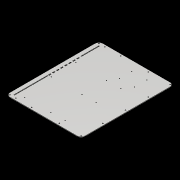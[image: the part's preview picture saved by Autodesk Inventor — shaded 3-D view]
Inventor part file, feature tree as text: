
AUTODESK INVENTOR PART (.ipt)
format: ipt  version: 2018.2 (Build 222227000, 227)  size: 322,560 bytes
history: native  units: mm
features: reference x21, other x7, extrude x7, sketch x7, projected_geometry x1
ambient origin geometry x8: Origin, YZ Plane, XZ Plane, XY Plane, X Axis, Y Axis, Z Axis, Center Point
bodies: Body1 (feature_tree)
feature tree (43):
  other  "ソリッド1"
  extrude  "押し出し1"  Depth=380.0mm
  extrude  "押し出し2"  Depth=470.0mm
  extrude  "押し出し3"  Depth=4.5mm
  extrude  "押し出し4"  Depth=10.0mm
  extrude  "押し出し5"  Depth=10.0mm
  extrude  "押し出し6"  Depth=10.0mm
  extrude  "押し出し7"  Depth=10.0mm
  sketch  "スケッチ1"
  sketch  "スケッチ2"
  reference  "参照1"
  reference  "参照2"
  reference  "参照3"
  reference  "参照4"
  reference  "参照5"
  reference  "参照6"
  reference  "参照7"
  reference  "参照8"
  reference  "参照9"
  sketch  "スケッチ4"
  reference  "参照10"
  reference  "参照11"
  reference  "参照12"
  reference  "参照13"
  reference  "参照14"
  reference  "参照15"
  reference  "参照16"
  reference  "参照17"
  reference  "参照18"
  reference  "参照19"
  sketch  "スケッチ5"
  sketch  "スケッチ6"
  projected_geometry  "投影ループ1"
  sketch  "スケッチ7"
  reference  "参照20"
  reference  "参照21"
  sketch  "スケッチ8"
  other  "<userpath>\Documents\CAD\eatx_case\layout.iam"
  other  "layout.iam"
  other  "Rampage V Extreme Assembly:1"
  other  "Rampage V Extreme PCB_1"
  other  "backpanel:1"
  other  "left_panel:1"
